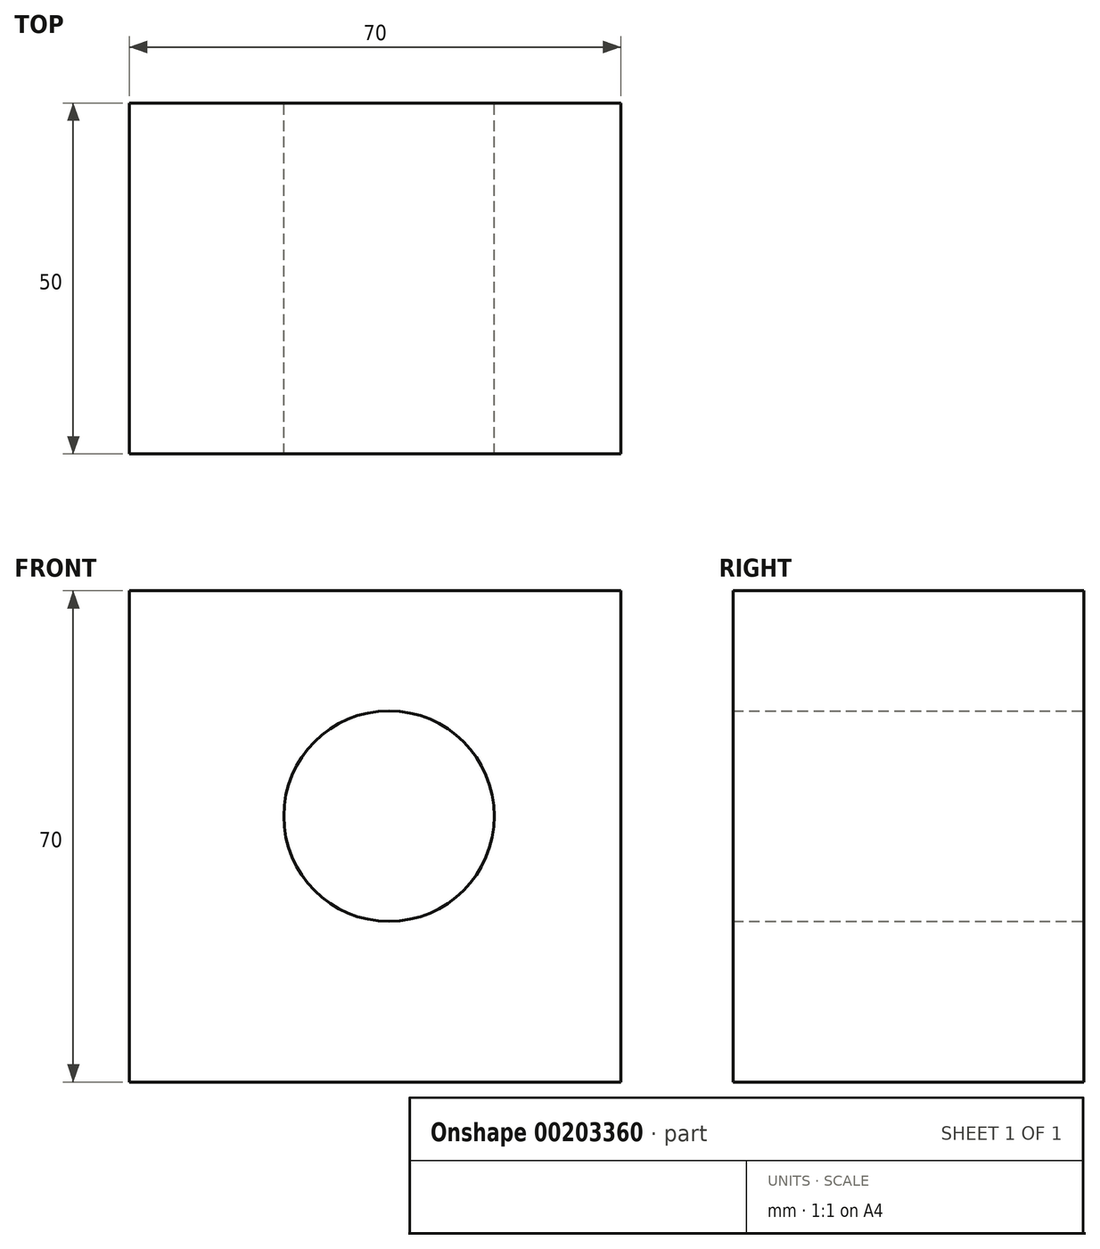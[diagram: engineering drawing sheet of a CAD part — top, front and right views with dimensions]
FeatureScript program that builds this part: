
annotation { "Feature Type Name" : "Feature", "Feature Type Description" : "" }
export const myFeature = defineFeature(function(context is Context, id is Id, definition is map)
    precondition{}
    {
        {
            var Q0;
            Q0=qCreatedBy(makeId("Front.planeOp"),FACE);
            var sketch = newSketch(context, id + "F0", { "sketchPlane" : qUnion([Q0])});
            skLineSegment(sketch, "E0.bottom", {"start": v(0, 0) * mm, "end": v(70, 0) * mm});
            skLineSegment(sketch, "E0.top", {"start": v(0, 70) * mm, "end": v(70, 70) * mm});
            skLineSegment(sketch, "E0.left", {"start": v(0, 0) * mm, "end": v(0, 70) * mm});
            skLineSegment(sketch, "E0.right", {"start": v(70, 0) * mm, "end": v(70, 70) * mm});
            skCircle(sketch, "E1", {"center": v(36.98, 37.88) * mm, "radius": 15 * mm});
            skSolve(sketch);
        }
        {
            var Q0;
            Q0=makeQuery(id+"F0.imprint","IMPRINT",FACE,{"disambiguationData":[TD([[makeQuery(id+"F0.imprint","IMPRINT",EDGE,{"derivedFrom":sQuery(id+"F0.wireOp",EDGE,"E0.bottom")}),1.0]])]});
            extrude(context, id + "F1", {"entities" : qUnion([Q0]), "depth" : 50 * mm, "offsetDistance" : 25 * mm});
        }
    });
